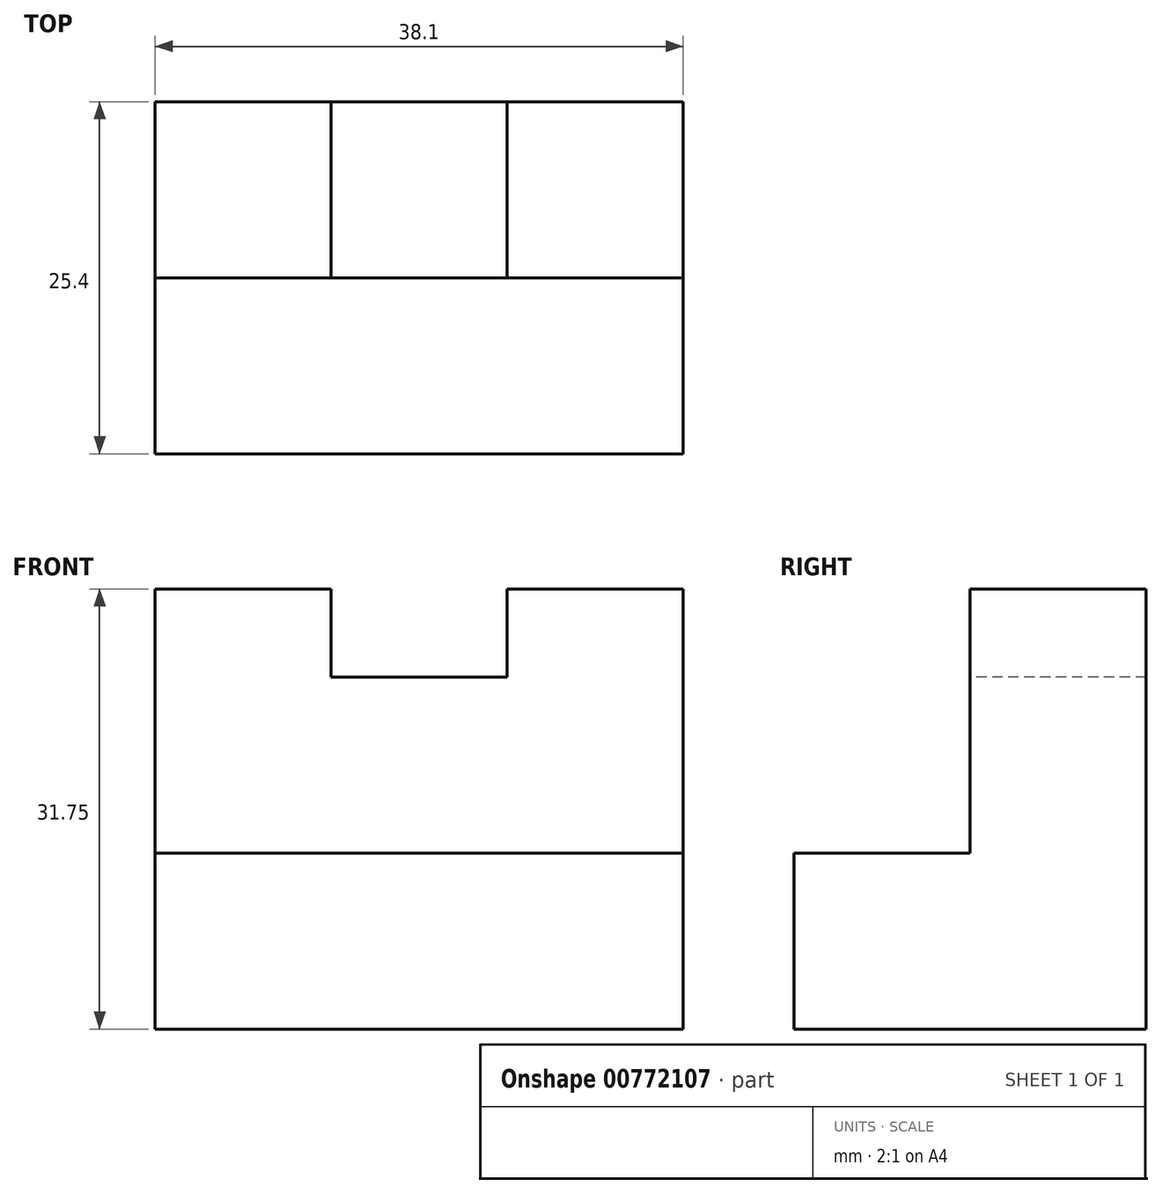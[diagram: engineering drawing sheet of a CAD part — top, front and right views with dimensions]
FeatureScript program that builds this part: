
annotation { "Feature Type Name" : "Feature", "Feature Type Description" : "" }
export const myFeature = defineFeature(function(context is Context, id is Id, definition is map)
    precondition{}
    {
        {
            var Q0;
            Q0=qCreatedBy(makeId("Right.planeOp"),FACE);
            var sketch = newSketch(context, id + "F0", { "sketchPlane" : qUnion([Q0])});
            skLineSegment(sketch, "E0", {"start": v(0, -2.22) * mm, "end": v(0, 10.48) * mm});
            skLineSegment(sketch, "E1", {"start": v(0, 10.48) * mm, "end": v(12.7, 10.48) * mm});
            skLineSegment(sketch, "E2", {"start": v(12.7, 10.48) * mm, "end": v(12.7, 29.53) * mm});
            skLineSegment(sketch, "E3", {"start": v(12.7, 29.53) * mm, "end": v(25.4, 29.53) * mm});
            skLineSegment(sketch, "E4", {"start": v(25.4, 29.53) * mm, "end": v(25.4, -2.22) * mm});
            skLineSegment(sketch, "E5", {"start": v(0, -2.22) * mm, "end": v(25.4, -2.22) * mm});
            skSolve(sketch);
        }
        {
            var Q0;
            Q0 = qSketchRegion(id + "F0", true);
            extrude(context, id + "F1", {"entities" : qUnion([Q0]), "depth" : 38.1 * mm, "offsetDistance" : 25.4 * mm});
        }
        {
            var Q0;
            Q0=makeQuery(id+"F1.opExtrude","SWEPT_FACE",FACE,{"disambiguationData":[OSD([sQuery(id+"F0.wireOp",EDGE,"E2")])]});
            var sketch = newSketch(context, id + "F2", { "sketchPlane" : qUnion([Q0])});
            skLineSegment(sketch, "E6", {"start": v(0, 29.53) * mm, "end": v(12.7, 29.53) * mm});
            skLineSegment(sketch, "E7", {"start": v(38.1, 29.53) * mm, "end": v(25.4, 29.53) * mm});
            skLineSegment(sketch, "E8", {"start": v(12.7, 29.53) * mm, "end": v(12.7, 23.18) * mm});
            skLineSegment(sketch, "E9", {"start": v(25.4, 29.53) * mm, "end": v(25.4, 23.18) * mm});
            skLineSegment(sketch, "E10", {"start": v(25.4, 23.18) * mm, "end": v(12.7, 23.18) * mm});
            skSolve(sketch);
        }
        {
            var Q0;
            {var subQ0=sQuery(id+"F2.wireOp",EDGE,"E8");Q0=makeQuery(id+"F2.imprint","IMPRINT",FACE,{"disambiguationData":[TD([[makeQuery(id+"F2.imprint","IMPRINT",EDGE,{"derivedFrom":subQ0}),1.0]])]});}
            extrude(context, id + "F3", {"entities" : qUnion([Q0]), "operationType" : NewBodyOperationType.REMOVE, "oppositeDirection" : true, "depth" : 25.4 * mm, "offsetDistance" : 25.4 * mm});
        }
    });
